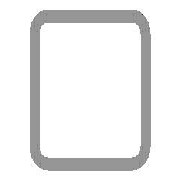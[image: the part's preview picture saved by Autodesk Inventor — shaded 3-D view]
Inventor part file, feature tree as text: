
AUTODESK INVENTOR PART (.ipt)
format: ipt  version: 2025.1 (Build 291241020, 241B)  size: 142,848 bytes
history: native  units: mm (DEFAULTED — no unit token found)
features: other x4, sketch x1, plane x1
ambient origin geometry x8: Origin, YZ Plane, XZ Plane, XY Plane, X Axis, Y Axis, Z Axis, Center Point
bodies: Solid1 (feature_tree), Body (feature_tree)
feature tree (6):
  parser-record x1  (decoder bookkeeping rows leaked as tree rows — omitted from the tree; the rows remain in map.json)
  other  "Driven Length"
  other  "Start Plane"
  other  "End Plane"
  sketch  "Sketch3"  dims[d3=2750.0mm d4=0.0mm d7=8.0mm d9=100.0mm d11=100.0mm d12=4.0mm d13=100.0mm d14=2850.0mm d15=50.0mm d16=50.0mm d17=90.0deg d18=2750.0mm]
  plane  "Work Plane3"
